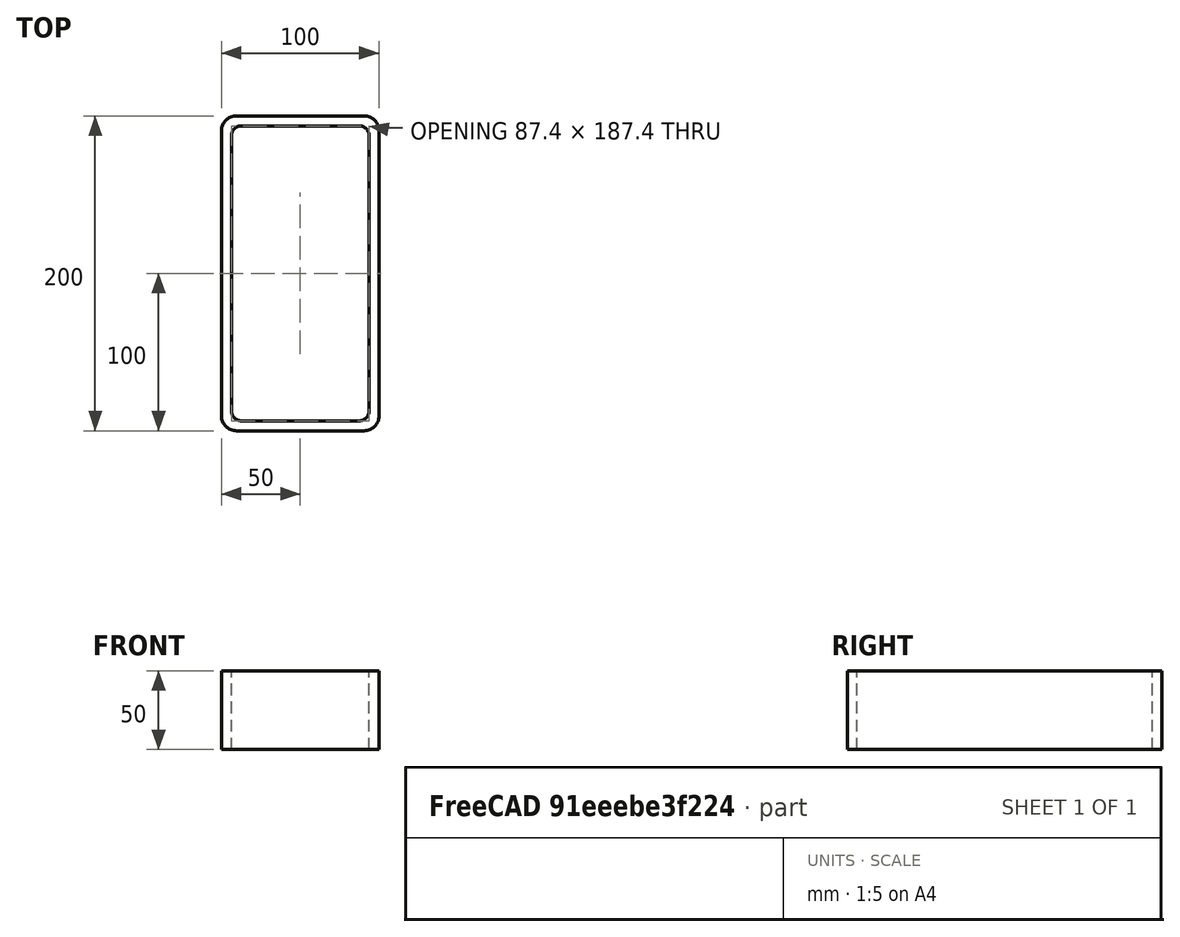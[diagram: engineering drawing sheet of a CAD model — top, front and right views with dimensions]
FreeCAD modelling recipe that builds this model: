
FCSTD DOCUMENT  (FreeCAD 0.15R4671 (Git))
Label: Rectangular hollow section 200x100x6.3 EN10219 S235JRH
License: All rights reserved
LicenseURL: http://en.wikipedia.org/wiki/All_rights_reserved
objects: Sketcher::SketchObject×1, Part::Extrusion×1
note: 2 computed .brp shape members not serialized (recipe doc carries the construction recipe); baked Part::Feature solids carry a one-line shape summary decoded from their .brp

FEATURE [Sketcher::SketchObject] Sketch
  sketch-geometry (16):
    g0: LineSegment StartX=-37.4 StartY=93.7 StartZ=0 EndX=37.4 EndY=93.7 EndZ=0
    g1: LineSegment StartX=43.7 StartY=87.4 StartZ=0 EndX=43.7 EndY=-87.4 EndZ=0
    g2: LineSegment StartX=37.4 StartY=-93.7 StartZ=0 EndX=-37.4 EndY=-93.7 EndZ=0
    g3: LineSegment StartX=-43.7 StartY=-87.4 StartZ=0 EndX=-43.7 EndY=87.4 EndZ=0
    g4: LineSegment StartX=-40.55 StartY=100 StartZ=0 EndX=40.55 EndY=100 EndZ=0
    g5: LineSegment StartX=50 StartY=90.55 StartZ=0 EndX=50 EndY=-90.55 EndZ=0
    g6: LineSegment StartX=40.55 StartY=-100 StartZ=0 EndX=-40.55 EndY=-100 EndZ=0
    g7: LineSegment StartX=-50 StartY=-90.55 StartZ=0 EndX=-50 EndY=90.55 EndZ=0
    g8: ArcOfCircle CenterX=-37.4 CenterY=87.4 CenterZ=0 NormalX=0 NormalY=0 NormalZ=1 Radius=6.3 StartAngle=1.5708 EndAngle=3.14159
    g9: ArcOfCircle CenterX=37.4 CenterY=87.4 CenterZ=0 NormalX=0 NormalY=0 NormalZ=1 Radius=6.3 StartAngle=0 EndAngle=1.5708
    g10: ArcOfCircle CenterX=37.4 CenterY=-87.4 CenterZ=0 NormalX=0 NormalY=0 NormalZ=1 Radius=6.3 StartAngle=4.71239 EndAngle=6.28319
    g11: ArcOfCircle CenterX=-37.4 CenterY=-87.4 CenterZ=0 NormalX=0 NormalY=0 NormalZ=1 Radius=6.3 StartAngle=3.14159 EndAngle=4.71239
    g12: ArcOfCircle CenterX=40.55 CenterY=90.55 CenterZ=0 NormalX=0 NormalY=0 NormalZ=1 Radius=9.45 StartAngle=0 EndAngle=1.5708
    g13: ArcOfCircle CenterX=40.55 CenterY=-90.55 CenterZ=0 NormalX=0 NormalY=0 NormalZ=1 Radius=9.45 StartAngle=4.71239 EndAngle=6.28319
    g14: ArcOfCircle CenterX=-40.55 CenterY=-90.55 CenterZ=0 NormalX=0 NormalY=0 NormalZ=1 Radius=9.45 StartAngle=3.14159 EndAngle=4.71239
    g15: ArcOfCircle CenterX=-40.55 CenterY=90.55 CenterZ=0 NormalX=0 NormalY=0 NormalZ=1 Radius=9.45 StartAngle=1.5708 EndAngle=3.14159
  constraints (36):
    c: Horizontal(g2)
    c: Vertical(g3)
    c: Horizontal(g6)
    c: Vertical(g7)
    c: Tangent(g3,g8) = 1.5708
    c: Tangent(g0,g8) = 1.5708
    c: Tangent(g0,g9) = 1.5708
    c: Tangent(g1,g9) = 1.5708
    c: Tangent(g1,g10) = 1.5708
    c: Tangent(g2,g10) = 1.5708
    c: Tangent(g2,g11) = 1.5708
    c: Tangent(g3,g11) = 1.5708
    c: Tangent(g4,g12) = 1.5708
    c: Tangent(g5,g12) = 1.5708
    c: Tangent(g5,g13) = 1.5708
    c: Tangent(g6,g13) = 1.5708
    c: Tangent(g6,g14) = 1.5708
    c: Tangent(g7,g14) = 1.5708
    c: Tangent(g7,g15) = 1.5708
    c: Tangent(g4,g15) = 1.5708
    c: Equal(g9,g8)
    c: Equal(g9,g11)
    c: Equal(g9,g10)
    c: Equal(g12,g15)
    c: Equal(g12,g14)
    c: Equal(g12,g13)
    c: Symmetric(g4,g6,g-1)
    c: Symmetric(g7,g5,g-2)
    c: DistanceY(g4,g6) = -200
    c: DistanceX(g7,g5) = 100
    c: Symmetric(g3,g1,g-2)
    c: Symmetric(g0,g2,g-1)
    c: DistanceY(g0,g4) = 6.3
    c: DistanceX(g5,g1) = -6.3
    c: Radius(g9) = 6.3
    c: Radius(g12) = 9.45
FEATURE [Part::Extrusion] Extrude  label="Rectangular hollow section 200x100x6.3 EN10219 S235JRH"
  Base = -> Sketch
  Dir = (0,0,50)
  Solid = true
